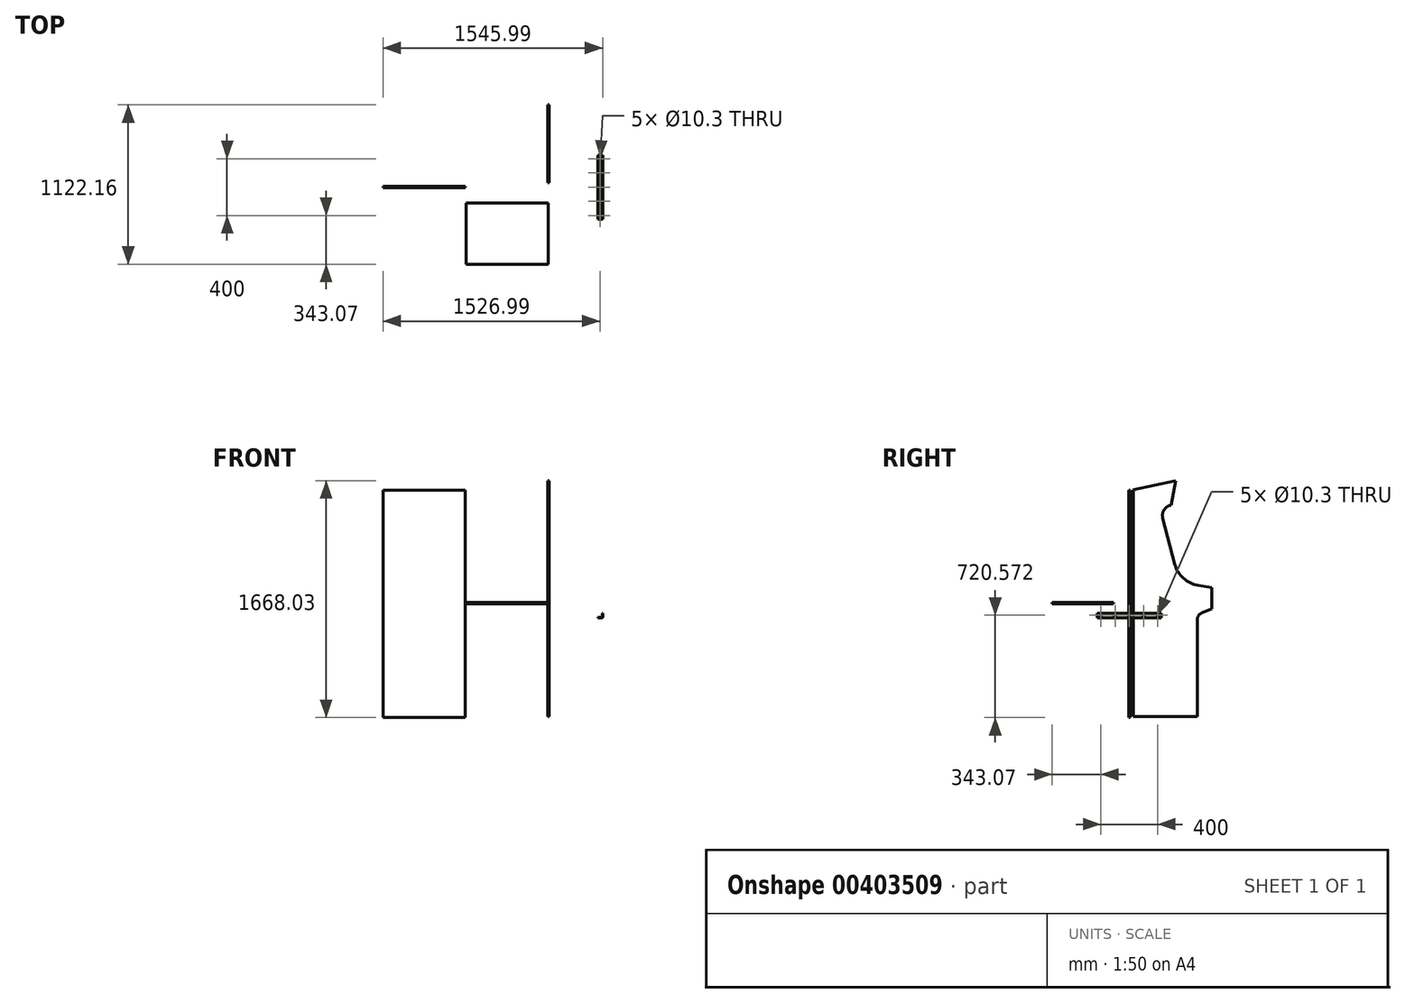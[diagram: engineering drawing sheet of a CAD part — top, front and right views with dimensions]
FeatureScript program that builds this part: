
annotation { "Feature Type Name" : "Feature", "Feature Type Description" : "" }
export const myFeature = defineFeature(function(context is Context, id is Id, definition is map)
    precondition{}
    {
        {
            var Q0;
            Q0=qCreatedBy(makeId("Right.planeOp"),FACE);
            var sketch = newSketch(context, id + "F0", { "sketchPlane" : qUnion([Q0])});
            skLineSegment(sketch, "E0", {"start": v(29.09, 799.78) * mm, "end": v(29.09, -800.22) * mm});
            skLineSegment(sketch, "E1", {"start": v(29.09, -800.22) * mm, "end": v(479.09, -800.22) * mm});
            skLineSegment(sketch, "E2", {"start": v(479.09, -800.22) * mm, "end": v(479.09, -115.45) * mm});
            skLineSegment(sketch, "E3", {"start": v(509.73, -69.36) * mm, "end": v(579.09, -40.22) * mm});
            skLineSegment(sketch, "E4", {"start": v(579.09, -40.22) * mm, "end": v(579.09, 110.78) * mm});
            skLineSegment(sketch, "E5", {"start": v(579.09, 110.78) * mm, "end": v(483.94, 125.62) * mm});
            skLineSegment(sketch, "E6", {"start": v(321.41, 272.14) * mm, "end": v(235.42, 597.58) * mm});
            skLineSegment(sketch, "E7", {"start": v(294.1, 690.46) * mm, "end": v(294.8, 690.6) * mm});
            skLineSegment(sketch, "E8", {"start": v(29.09, 799.78) * mm, "end": v(326.09, 861.78) * mm});
            skLineSegment(sketch, "E9", {"start": v(326.09, 861.78) * mm, "end": v(294.8, 690.6) * mm});
            skPoint(sketch, "E10.visualSharp", {"position": v(479.09, -82.22) * mm});
            skArc(sketch, "E10.filletArc", {"start": v(509.73, -69.36) * mm, "mid": v(487.45, -87.78) * mm, "end": v(479.09, -115.45) * mm});
            skPoint(sketch, "E11.visualSharp", {"position": v(214.8, 675.6) * mm});
            skArc(sketch, "E11.filletArc", {"start": v(294.1, 690.46) * mm, "mid": v(244.52, 656.81) * mm, "end": v(235.42, 597.58) * mm});
            skPoint(sketch, "E12.visualSharp", {"position": v(354.8, 145.78) * mm});
            skArc(sketch, "E12.filletArc", {"start": v(321.41, 272.14) * mm, "mid": v(380.86, 174.68) * mm, "end": v(483.94, 125.62) * mm});
            skSolve(sketch);
        }
        {
            var Q0;
            Q0=makeQuery(id+"F0.imprint","IMPRINT",FACE,{"disambiguationData":[TD([[makeQuery(id+"F0.imprint","IMPRINT",EDGE,{"derivedFrom":sQuery(id+"F0.wireOp",EDGE,"E0")}),1.0]])]});
            extrude(context, id + "F1", {"entities" : qUnion([Q0]), "endBound" : BoundingType.SYMMETRIC, "depth" : 10 * mm});
        }
        {
            var Q0;
            Q0=qCreatedBy(makeId("Top.planeOp"),FACE);
            var sketch = newSketch(context, id + "F2", { "sketchPlane" : qUnion([Q0])});
            skLineSegment(sketch, "E13.bottom", {"start": v(0, -113.07) * mm, "end": v(-580, -113.07) * mm});
            skLineSegment(sketch, "E13.top", {"start": v(0, -543.07) * mm, "end": v(-580, -543.07) * mm});
            skLineSegment(sketch, "E13.left", {"start": v(0, -113.07) * mm, "end": v(0, -543.07) * mm});
            skLineSegment(sketch, "E13.right", {"start": v(-580, -113.07) * mm, "end": v(-580, -543.07) * mm});
            skSolve(sketch);
        }
        {
            var Q0;
            Q0=makeQuery(id+"F2.imprint","IMPRINT",FACE,{"disambiguationData":[TD([[makeQuery(id+"F2.imprint","IMPRINT",EDGE,{"derivedFrom":sQuery(id+"F2.wireOp",EDGE,"E13.bottom")}),1.0]])]});
            extrude(context, id + "F3", {"entities" : qUnion([Q0]), "endBound" : BoundingType.SYMMETRIC, "depth" : 10 * mm});
        }
        {
            var Q0;
            Q0=qCreatedBy(makeId("Front.planeOp"),FACE);
            var sketch = newSketch(context, id + "F4", { "sketchPlane" : qUnion([Q0])});
            skLineSegment(sketch, "E14", {"start": v(378.97, -71.68) * mm, "end": v(378.97, -101.68) * mm});
            skLineSegment(sketch, "E15", {"start": v(378.97, -101.68) * mm, "end": v(348.97, -101.68) * mm});
            skLineSegment(sketch, "E16.0", {"start": v(381.97, -104.68) * mm, "end": v(348.97, -104.68) * mm});
            skLineSegment(sketch, "E16.1", {"start": v(381.97, -71.68) * mm, "end": v(381.97, -104.68) * mm});
            skLineSegment(sketch, "E17", {"start": v(381.97, -71.68) * mm, "end": v(378.97, -71.68) * mm});
            skLineSegment(sketch, "E18", {"start": v(348.97, -104.68) * mm, "end": v(348.97, -101.68) * mm});
            skSolve(sketch);
        }
        {
            var Q0;
            Q0=makeQuery(id+"F4.imprint","IMPRINT",FACE,{"disambiguationData":[TD([[makeQuery(id+"F4.imprint","IMPRINT",EDGE,{"derivedFrom":sQuery(id+"F4.wireOp",EDGE,"E14")}),1.0]])]});
            extrude(context, id + "F5", {"entities" : qUnion([Q0]), "endBound" : BoundingType.SYMMETRIC, "depth" : 450 * mm});
        }
        {
            var Q0;
            Q0=makeQuery(id+"F5.opExtrude","SWEPT_EDGE",EDGE,{"disambiguationData":[OSD([sQuery(id+"F4.wireOp",EDGE,"E16.0"),sQuery(id+"F4.wireOp",EDGE,"E16.1")])]});
            var Q1;
            Q1=makeQuery(id+"F5.opExtrude","SWEPT_EDGE",EDGE,{"disambiguationData":[OSD([sQuery(id+"F4.wireOp",EDGE,"E14"),sQuery(id+"F4.wireOp",EDGE,"E15")])]});
            fillet(context, id + "F6", {"entities" : qUnion([Q0, Q1]), "radius" : 5 * mm, "tangentPropagation" : true, "allowEdgeOverflow" : false});
        }
        {
            var Q0;
            Q0=makeQuery(id+"F5.opExtrude","SWEPT_FACE",FACE,{"disambiguationData":[OSD([sQuery(id+"F4.wireOp",EDGE,"E16.1")])]});
            var sketch = newSketch(context, id + "F7", { "sketchPlane" : qUnion([Q0])});
            skCircle(sketch, "E19", {"center": v(-200, -85.68) * mm, "radius": 5.15 * mm});
            skPoint(sketch, "E19.centerSnap0", {"position": v(-225, -85.68) * mm});
            skCircle(sketch, "E20", {"center": v(200, -85.68) * mm, "radius": 5.15 * mm});
            skPoint(sketch, "E21", {"position": v(225, -85.68) * mm});
            skCircle(sketch, "E22", {"center": v(0, -85.68) * mm, "radius": 5.15 * mm});
            skCircle(sketch, "E23", {"center": v(-100, -85.68) * mm, "radius": 5.15 * mm});
            skCircle(sketch, "E24", {"center": v(100, -85.68) * mm, "radius": 5.15 * mm});
            skSolve(sketch);
        }
        {
            var Q0;
            Q0=makeQuery(id+"F7.imprint","IMPRINT",FACE,{"disambiguationData":[TD([[makeQuery(id+"F7.imprint","IMPRINT",EDGE,{"derivedFrom":sQuery(id+"F7.wireOp",EDGE,"E20")}),1.0]])]});
            var Q1;
            Q1=makeQuery(id+"F7.imprint","IMPRINT",FACE,{"disambiguationData":[TD([[makeQuery(id+"F7.imprint","IMPRINT",EDGE,{"derivedFrom":sQuery(id+"F7.wireOp",EDGE,"E22")}),1.0]])]});
            var Q2;
            Q2=makeQuery(id+"F7.imprint","IMPRINT",FACE,{"disambiguationData":[TD([[makeQuery(id+"F7.imprint","IMPRINT",EDGE,{"derivedFrom":sQuery(id+"F7.wireOp",EDGE,"E23")}),1.0]])]});
            var Q3;
            Q3=makeQuery(id+"F7.imprint","IMPRINT",FACE,{"disambiguationData":[TD([[makeQuery(id+"F7.imprint","IMPRINT",EDGE,{"derivedFrom":sQuery(id+"F7.wireOp",EDGE,"E24")}),1.0]])]});
            var Q4;
            Q4=makeQuery(id+"F7.imprint","IMPRINT",FACE,{"disambiguationData":[TD([[makeQuery(id+"F7.imprint","IMPRINT",EDGE,{"derivedFrom":sQuery(id+"F7.wireOp",EDGE,"E19")}),1.0]])]});
            extrude(context, id + "F8", {"entities" : qUnion([Q0, Q1, Q2, Q3, Q4]), "operationType" : NewBodyOperationType.REMOVE, "endBound" : BoundingType.UP_TO_NEXT, "oppositeDirection" : true, "depth" : 25 * mm});
        }
        {
            var Q0;
            Q0=makeQuery(id+"F5.opExtrude","SWEPT_FACE",FACE,{"disambiguationData":[OSD([sQuery(id+"F4.wireOp",EDGE,"E16.0")])]});
            var sketch = newSketch(context, id + "F9", { "sketchPlane" : qUnion([Q0])});
            skCircle(sketch, "E25", {"center": v(362.97, 200) * mm, "radius": 5.15 * mm});
            skPoint(sketch, "E25.centerSnap0", {"position": v(362.97, 225) * mm});
            skCircle(sketch, "E26", {"center": v(362.97, 100) * mm, "radius": 5.15 * mm});
            skCircle(sketch, "E27", {"center": v(362.97, 0) * mm, "radius": 5.15 * mm});
            skCircle(sketch, "E28", {"center": v(362.97, -100) * mm, "radius": 5.15 * mm});
            skCircle(sketch, "E29", {"center": v(362.97, -200) * mm, "radius": 5.15 * mm});
            skSolve(sketch);
        }
        {
            var Q0;
            Q0=makeQuery(id+"F9.imprint","IMPRINT",FACE,{"disambiguationData":[TD([[makeQuery(id+"F9.imprint","IMPRINT",EDGE,{"derivedFrom":sQuery(id+"F9.wireOp",EDGE,"E25")}),1.0]])]});
            var Q1;
            Q1=makeQuery(id+"F9.imprint","IMPRINT",FACE,{"disambiguationData":[TD([[makeQuery(id+"F9.imprint","IMPRINT",EDGE,{"derivedFrom":sQuery(id+"F9.wireOp",EDGE,"E26")}),1.0]])]});
            var Q2;
            Q2=makeQuery(id+"F9.imprint","IMPRINT",FACE,{"disambiguationData":[TD([[makeQuery(id+"F9.imprint","IMPRINT",EDGE,{"derivedFrom":sQuery(id+"F9.wireOp",EDGE,"E27")}),1.0]])]});
            var Q3;
            Q3=makeQuery(id+"F9.imprint","IMPRINT",FACE,{"disambiguationData":[TD([[makeQuery(id+"F9.imprint","IMPRINT",EDGE,{"derivedFrom":sQuery(id+"F9.wireOp",EDGE,"E28")}),1.0]])]});
            var Q4;
            Q4=makeQuery(id+"F9.imprint","IMPRINT",FACE,{"disambiguationData":[TD([[makeQuery(id+"F9.imprint","IMPRINT",EDGE,{"derivedFrom":sQuery(id+"F9.wireOp",EDGE,"E29")}),1.0]])]});
            extrude(context, id + "F10", {"entities" : qUnion([Q0, Q1, Q2, Q3, Q4]), "operationType" : NewBodyOperationType.REMOVE, "endBound" : BoundingType.UP_TO_NEXT, "oppositeDirection" : true, "depth" : 25 * mm});
        }
        {
            var Q0;
            Q0=qCreatedBy(makeId("Front.planeOp"),FACE);
            var sketch = newSketch(context, id + "F11", { "sketchPlane" : qUnion([Q0])});
            skLineSegment(sketch, "E30.bottom", {"start": v(-1164.02, -806.25) * mm, "end": v(-584.02, -806.25) * mm});
            skLineSegment(sketch, "E30.top", {"start": v(-1164.02, 793.75) * mm, "end": v(-584.02, 793.75) * mm});
            skLineSegment(sketch, "E30.left", {"start": v(-1164.02, -806.25) * mm, "end": v(-1164.02, 793.75) * mm});
            skLineSegment(sketch, "E30.right", {"start": v(-584.02, -806.25) * mm, "end": v(-584.02, 793.75) * mm});
            skSolve(sketch);
        }
        {
            var Q0;
            Q0=makeQuery(id+"F11.imprint","IMPRINT",FACE,{"disambiguationData":[TD([[makeQuery(id+"F11.imprint","IMPRINT",EDGE,{"derivedFrom":sQuery(id+"F11.wireOp",EDGE,"E30.bottom")}),1.0]])]});
            extrude(context, id + "F12", {"entities" : qUnion([Q0]), "endBound" : BoundingType.SYMMETRIC, "depth" : 10 * mm});
        }
    });
